# Revit family: Zumtobel SLOTLIGHT INF II MRT
name_source: partatom
category: Lighting Fixtures
revit_build: Autodesk Revit 2018 (Build: 20170223_1515(x64)
units: mm (PartAtom-declared; Revit-internal decimal feet)

## family parameters
Cut with Voids When Loaded = No
Host = Face
Light Source = Yes
OmniClass Number = 23.80.70.11
OmniClass Title = Luminaries for Internal Lighting
Part Type = Normal
Room Calculation Point = No
Round Connector Dimension = Use Diameter
Shared = No

## types (10) — shared parameters
Assembly Code = D5020200
Color Filter = 16777215
Color Light Emitting Surface = Zumtobel_PMMA_White
Description = SLOTLIGHT Infinity II MRT
Dimming Lamp Color Temperature Shift = <None>
Emit Shape Visible in Rendering = No
Emit from Rectangle Length = 75 mm
Height = 136 mm
Lamp = LED
Manufacturer = Zumtobel Lighting
Tilt Angle = -90.00°
URL = http://www.zumtobel.com
Width = 80 mm  [stored 0.262467 ft]
zero-valued in all types: Default Elevation

## per-type parameters (varying)
| type | Apparent Load | Emit from Rectangle Width | Length | Minicell | Model | Photometric Web File | SLN2-B |
| SLN2 MRT 1600-840 L1000 PC/PCO/DD LDE | 14 VA | 1000 mm  [stored 3.28084 ft] | 1000 mm  [stored 3.28084 ft] | No | 42189218+ 22903533 | 42189218_(840PC-4000K-diffuse_LEO).IES | Yes |
| SLN2 MRT 1600-840 L1250 PC/PCO/DD LDE | 16 VA | 1250 mm  [stored 4.10105 ft] | 1250 mm  [stored 4.10105 ft] | No | 42189219+ 22903534 | 42189219_(840PC-4000K-diffuse_LEO).IES | Yes |
| SLN2 MRT 1600-840 L1500 PC/PCO/DD LDE | 19 VA | 1500 mm  [stored 4.92126 ft] | 1500 mm  [stored 4.92126 ft] | No | 42189220+ 22903535 | 42189220_(840PC-4000K-diffuse_LEO).IES | Yes |
| SLN2 MRT 1600-840 L1750 PC/PCO/DD LDE | 22 VA | 1750 mm  [stored 5.74147 ft] | 1750 mm  [stored 5.74147 ft] | No | 42189221+ 22903536 | 42189221_(840PC-4000K-diffuse_LEO).IES | Yes |
| SLN2 MRT 1600-840 L2000 PC/PCO/DD LDE | 25 VA | 2000 mm | 2000 mm | No | 42189222+ 22903537 | 42189222_(840PC-4000K-diffuse_LEO).IES | Yes |
| SLN2 MRT 3500-840 L1000 MC LDE WHM | 27 VA | 1000 mm  [stored 3.28084 ft] | 1000 mm  [stored 3.28084 ft] | Yes | 42945583+22172162 | 42945583_(STD_LEO).IES | No |
| SLN2 MRT 3500-840 L1250 MC LDE WHM | 33 VA | 1250 mm  [stored 4.10105 ft] | 1250 mm  [stored 4.10105 ft] | Yes | 42945727+22172163 | 42945727_(STD_LEO).IES | No |
| SLN2 MRT 3500-840 L1500 MC LDE WHM | 41 VA | 1500 mm  [stored 4.92126 ft] | 1500 mm  [stored 4.92126 ft] | Yes | 42945700+22172164 | 42945700_(STD_LEO).IES | No |
| SLN2 MRT 3500-840 L1750 MC LDE WHM | 47 VA | 1750 mm  [stored 5.74147 ft] | 1750 mm  [stored 5.74147 ft] | Yes | 42945723+22172165 | 42945723_(STD_LEO).IES | No |
| SLN2 MRT 3500-840 L2000 MC LDE WHM | 54 VA | 2000 mm | 2000 mm | Yes | 42945746+22172166 | 42945746_(STD_LEO).IES | No |

note: [stored X ft] marks values corroborated as IEEE doubles in the binary element streams (Revit-internal decimal feet)

## geometry (parser evidence)
native form markers: Sweep x6
no freeform markers — native parametric forms only
